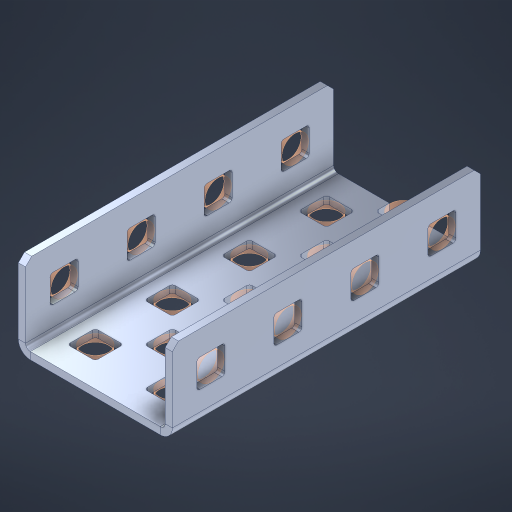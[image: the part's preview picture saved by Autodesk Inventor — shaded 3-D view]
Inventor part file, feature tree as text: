
AUTODESK INVENTOR PART (.ipt)
format: ipt  version: 2023 (Build 270158000, 158)  size: 599,552 bytes
history: native  units: in
note: dims shown in document units (in); Inventor stores cm internally (conversion verified against a paired STEP export)
features: other x27, extrude x18, sheet_metal_op x11, sketch x10, pattern_linear x2, mirror x1, chamfer x1
ambient origin geometry x8: Origin, YZ Plane, XZ Plane, XY Plane, X Axis, Y Axis, Z Axis, Center Point
bodies: Solid1 (feature_tree), Body (feature_tree)
feature tree (70):
  sheet_metal_op  "Flanges"
  other  "Flange Pattern Plane"
  other  "Flange Pattern Sketch"
  sheet_metal_op  "Flange Pattern"
  sheet_metal_op  "Body Pattern"
  pattern_linear  "Center Pattern"  Spacing1=0.0469in  [1 undecoded]
  other  "Arc Length"
  mirror  "Notch Mirror"
  pattern_linear  "Notch Pattern"  Spacing1=0.182in  [1 undecoded]
  chamfer  "End Chamfer"
  extrude  "Half Cut"  Depth=0.02in
  sketch  "Sketch1"  dims[d0=1.0in]
  other  "Plate1"
  sketch  "Sketch2"  dims[d1=2.0in]
  other  "Plate2"
  sheet_metal_op  "Bend1"
  sheet_metal_op  "Corner1"
  sketch  "Sketch3"  dims[d2=0.0469in]
  sketch  "Sketch7"  dims[d3=0.0469in]
  other  "Srf1"
  other  "Srf2"
  sketch  "Sketch8"  dims[d4=0.0234in]
  sketch  "Sketch9"  dims[d5=0.0938in]
  other  "Srf91"
  sheet_metal_op  "Body Pattern Sketch"
  other  "Srf92"
  sketch  "Sketch13"  dims[d6=0.0469in]
  sketch  "Sketch14"  dims[d7=0.5in d8=90.0deg d9=0.0312in]
  sketch  "Sketch15"  dims[d10=0.1875in]
  sketch  "Sketch16"  dims[d11=0.0469in d12=0.0469in d16=0.182in d17=0.02in d18=0.0469in d19=0.0in d20=0.25in d21=0.25in d38=1.5748in d40=0.5in d41=0.7874in d43=1.0in d46=0.172in d47=1.0in d48=0.0in d49=0.182in d50=0.02in d51=0.25in d52=0.25in d53=0.0469in d54=0.0in d55=0.172in d56=1.0in d57=0.0in d58=0.25in d60=1.5748in d62=0.5in d63=0.7874in d65=0.5in d85=0.1227in d86=0.1659in d88=0.04in d89=0.0469in d90=0.0in d91=0.04in d92=0.0491in d95=2.5in d96=0.04in d97=0.25in d98=45.0deg d99=0.25in d100=0.5in d101=0.0in d102=2.497in d106=0.182in d107=0.02in d108=0.5in d109=0.5in d110=0.0469in d111=0.0in d112=0.172in d113=0.5in d114=0.0in d117=0.5in d118=0.5in d119=0.5in]
  other  "Srf786"
  other  "Srf823"
  other  "Srf824"
  other  "Srf825"
  other  "Srf826"
  other  "Srf827"
  other  "Srf828"
  other  "Srf856"
  other  "Srf857"
  other  "Srf858"
  other  "Srf859"
  other  "Srf860"
  other  "Srf861"
  other  "Srf889"
  other  "Srf890"
  other  "Srf891"
  sheet_metal_op  "Flange Stamp"
  sheet_metal_op  "Flange Circle"
  sheet_metal_op  "Body Stamp"
  sheet_metal_op  "Body Circle"
  other  "Center Stamp"
  other  "Center Circle"
  sheet_metal_op  "Notch"
  extrude  "ExtrusionSrf2"  Depth=0.0469in
  extrude  "ExtrusionSrf92"  TaperAngle=0.0deg  [1 undecoded]
  extrude  "ExtrusionSrf823"  Depth=0.25in
  extrude  "ExtrusionSrf824"  Depth=0.25in
  extrude  "ExtrusionSrf825"  Depth=0.5in
  extrude  "ExtrusionSrf826"  Depth=0.5in
  extrude  "ExtrusionSrf827"  Depth=1.0in TaperAngle=0.0deg
  extrude  "ExtrusionSrf828"  Depth=0.182in
  extrude  "ExtrusionSrf856"  Depth=0.02in
  extrude  "ExtrusionSrf857"  Depth=0.25in
  extrude  "ExtrusionSrf858"  Depth=0.25in
  extrude  "ExtrusionSrf859"  Depth=0.0469in
  extrude  "ExtrusionSrf860"  TaperAngle=0.0deg  [1 undecoded]
  extrude  "ExtrusionSrf861"  Depth=0.5in
  extrude  "ExtrusionSrf889"  Depth=1.0in TaperAngle=0.0deg
  extrude  "ExtrusionSrf890"  Depth=0.25in
  extrude  "ExtrusionSrf891"  Depth=0.5in
note: 4 required parameter values undecoded (feature->parameter linkage not recoverable at this tier; creation-order binding heuristic only, values carry confidence <= 0.55)
